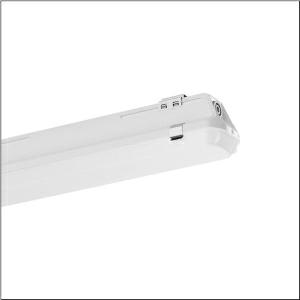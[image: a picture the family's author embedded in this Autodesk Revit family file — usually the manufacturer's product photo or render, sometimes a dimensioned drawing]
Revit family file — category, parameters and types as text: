
# Revit family: monsun_r__21_51fb10mp480b_b142
name_source: partatom
category: Lighting Fixtures
units: mm (PartAtom-declared; Revit-internal decimal feet)

## family parameters
Cut with Voids When Loaded = No
Host = Face
Light Source = No
Part Type = Normal
Room Calculation Point = No
Round Connector Dimension = Use Diameter
Shared = No

## types (1)
- --- (1 x LED, 8190 lm, 53.6 W, 4000K)
    Apparent Load = 54 VA
    CIE Flux Codes = 47 77 93 94 100
    Color Rendering = 80
    Color Temperature = 4000K
    Default Elevation = 1800 mm
    Description = Monsun® 21, damp-proof luminaire, chain hanger, primary optical cover: enclosure, of PMMA, light emission: direct distribution, primary light characteristic: symmetric, installation type: suspended mounting, surface-mounted, horizontal mounting, vertical mounting, LED, rated luminous flux: 8.190lm, luminous efficacy: 153lm/W, light colour: 840, colour temperature: 4000K, control gear: ECG, with terminal, 3-pole, max. 2.5mm², mains connection: 220..240V, AC, 50/60Hz, rated input power: 54W, housing, of glass-fibre reinforced polyester, uncoated, bright grey, incl. chain hanger, length: 1.590mm, width: 90mm, height: 88mm, clip for enclosure, of stainless steel (V2A), ceiling mounting element, of stainless steel (V2A), chain hanger, of stainless steel (V2A), protection rating (complete): IP66, insulation class (complete): insulation class I (protective earthing), certification: CE, ENEC, VDE, UKCA, protection symbol: D, impact resistance: IK04, permissible operating ambient temperature: -25..+35°C, standard: EN 50419, EN 60598-2-1, corresponds to IFS (International Featured Standards) requirements for safety and quality in the food industry, for indoor or canopied outdoor use, no direct snow, no direct sun, no direct rain, contact your sales advisor before using the luminaires in applications with unclear chemical exposure, large temperature fluctuations or condensation-forming humidity, LABS conformity tested according to VDMA 24364:2018-05, packaging unit: 1 piece
    Height = 89 mm
    Lamp = 1 x LED
    Lamp Light Flux = 8190 lm
    Lamp Power = 53.6 W
    Lamp count = 1
    Length = 1590 mm
    Luminous efficacy = 153 lm/W
    Manufacturer = Siteco
    ModVariant = No
    Model = 51FB10MP480B
    Mounting Place = Ceiling
    Mounting Type = Surface mounted
    Number of Poles = 1
    OnlyDefault = Yes
    Power Factor = 1
    Product Name = Monsun® 21
    Product group = damp-proof luminaire
    ProductGroupID = 301
    Protection Class = Protection class I
    Protection Degree = IP 66
    RLX_Detail_Level = 1
    RLX_Emergency_Light_Flux = 0 lm
    RLX_Emergency_Type = 0
    RLX_Emergency_Type_DB = No
    RlxData = <blob elided: 89869 chars, md5=4a58f4c1>
    Socket = socket
    Standby Power = 0 W
    System Light Flux = 8190 lm
    System Power = 54 W
    Type Comments = factory setting: luminous flux: 100 % | (A | C | E) | 121 mA
    Type Image = l_1006717.jpg
    URL = http://relux.com
    VarID = @adj_096983
    Voltage = 0 V
    Weight = 0.00 kg
    Width = 90 mm

## geometry (parser evidence)
native form markers: Blend x4, Sweep x13
no freeform markers — native parametric forms only
